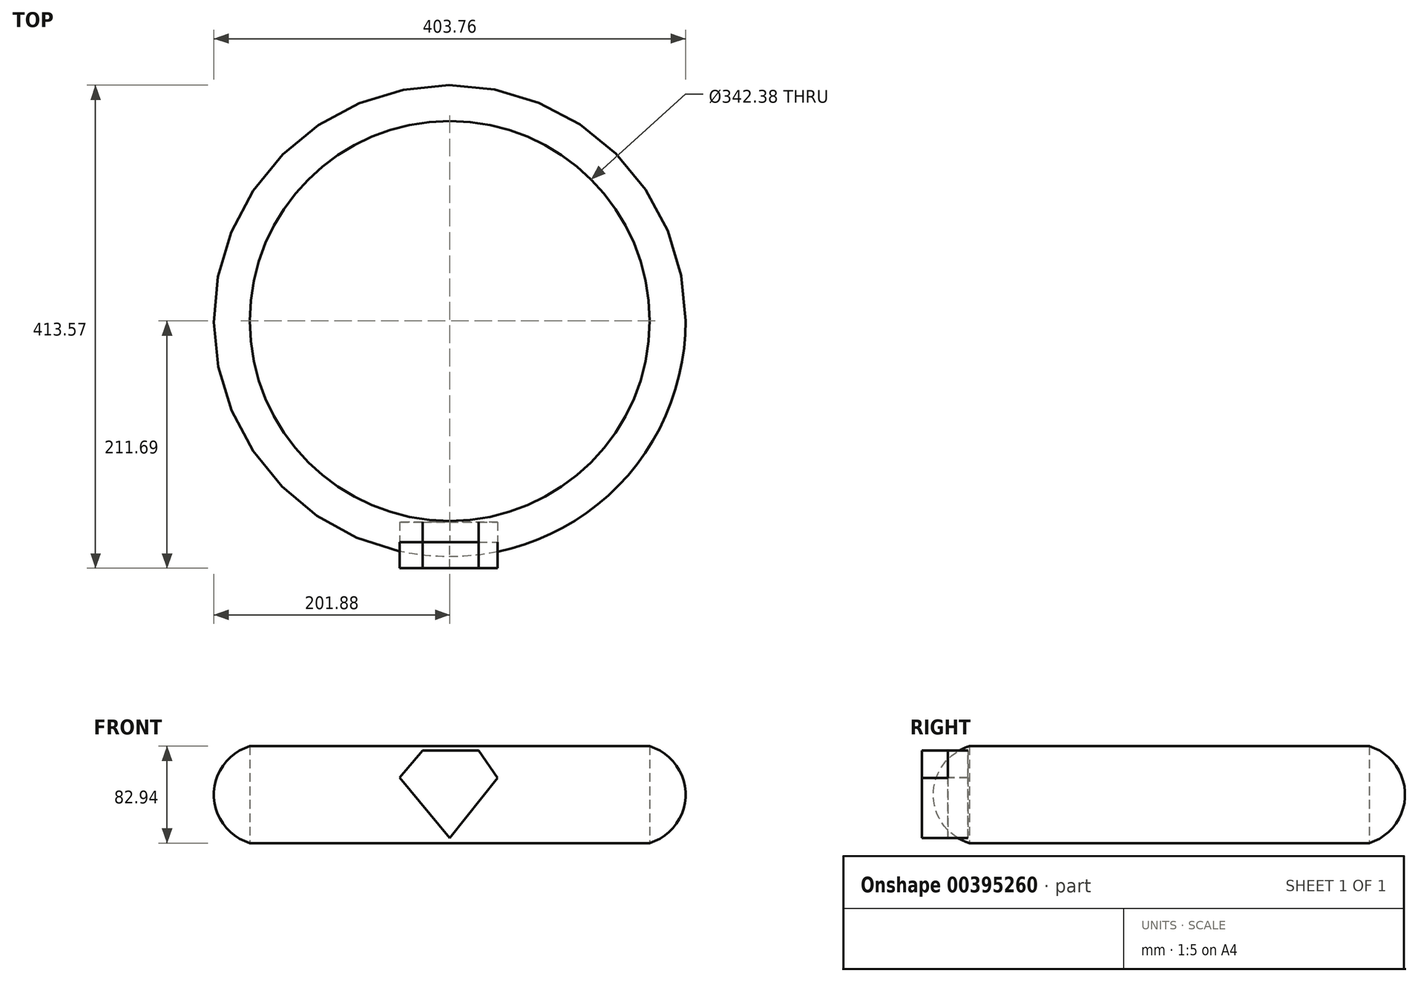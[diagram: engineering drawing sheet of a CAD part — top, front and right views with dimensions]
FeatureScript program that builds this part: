
annotation { "Feature Type Name" : "Feature", "Feature Type Description" : "" }
export const myFeature = defineFeature(function(context is Context, id is Id, definition is map)
    precondition{}
    {
        {
            var Q0;
            Q0=qCreatedBy(makeId("Top.planeOp"),FACE);
            var sketch = newSketch(context, id + "F0", { "sketchPlane" : qUnion([Q0])});
            skCircle(sketch, "E0", {"center": v(0, 0) * mm, "radius": 206.66 * mm});
            skSolve(sketch);
        }
        {
            var Q0;
            Q0=qCreatedBy(makeId("Right.planeOp"),FACE);
            var sketch = newSketch(context, id + "F1", { "sketchPlane" : qUnion([Q0])});
            skCircle(sketch, "E1", {"center": v(-158.53, 0) * mm, "radius": 43.36 * mm});
            skSolve(sketch);
        }
        {
            var Q0;
            Q0=makeQuery(id+"F1.imprint","IMPRINT",FACE,{"disambiguationData":[TD([[makeQuery(id+"F1.imprint","IMPRINT",EDGE,{"derivedFrom":sQuery(id+"F1.wireOp",EDGE,"E1")}),1.0]])]});
            var Q1;
            Q1=sQuery(id+"F0.wireOp",EDGE,"E0");
            sweep(context, id + "F2", {"profiles" : qUnion([Q0]), "path" : qUnion([Q1])});
        }
        {
            var Q0;
            Q0=qCreatedBy(makeId("Top.planeOp"),FACE);
            var sketch = newSketch(context, id + "F3", { "sketchPlane" : qUnion([Q0])});
            skCircle(sketch, "E2", {"center": v(0, 0) * mm, "radius": 171.19 * mm});
            skSolve(sketch);
        }
        {
            var Q0;
            Q0=qSketchRegion(id+"F3",true);
            extrude(context, id + "F4", {"entities" : qUnion([Q0]), "operationType" : NewBodyOperationType.REMOVE, "depth" : 439.93 * mm, "hasSecondDirection" : true, "secondDirectionOppositeDirection" : true, "secondDirectionDepth" : 259.08 * mm});
        }
        {
            var Q0;
            Q0=qCreatedBy(makeId("Top.planeOp"),FACE);
            var sketch = newSketch(context, id + "F5", { "sketchPlane" : qUnion([Q0])});
            skLineSegment(sketch, "E3", {"start": v(-284, -44.23) * mm, "end": v(-276.12, -35.04) * mm});
            skLineSegment(sketch, "E4", {"start": v(-276.12, -35.04) * mm, "end": v(-257.04, -35.04) * mm});
            skLineSegment(sketch, "E5", {"start": v(-257.04, -35.04) * mm, "end": v(-250.46, -44.36) * mm});
            skLineSegment(sketch, "E6", {"start": v(-250.46, -44.36) * mm, "end": v(-266.84, -65) * mm});
            skLineSegment(sketch, "E7", {"start": v(-266.84, -65) * mm, "end": v(-284, -44.23) * mm});
            skSolve(sketch);
        }
        {
            var Q0;
            Q0=qSketchRegion(id+"F5",true);
            extrude(context, id + "F6", {"entities" : qUnion([Q0]), "depth" : 8.9 * mm});
        }
        {
            var Q0;
            Q0=makeQuery(id+"F6.opExtrude","SWEPT_BODY",BODY,{"disambiguationData":[OSD([sQuery(id+"F5.wireOp",EDGE,"E3"),sQuery(id+"F5.wireOp",EDGE,"E4"),sQuery(id+"F5.wireOp",EDGE,"E5"),sQuery(id+"F5.wireOp",EDGE,"E6"),sQuery(id+"F5.wireOp",EDGE,"E7")])]});
            var Q1;
            Q1=makeQuery(id+"F6.opExtrude","CAP_EDGE",EDGE,{"disambiguationData":[OSD([sQuery(id+"F5.wireOp",EDGE,"E4")])],"isStart":false});
            transform(context, id + "F7", {"entities" : qUnion([Q0]), "transformType" : TransformType.ROTATION, "transformAxis" : qUnion([Q1]), "angle" : 90 * degree, "makeCopy" : false});
        }
        {
            var Q0;
            Q0=makeQuery(id+"F6.opExtrude","SWEPT_BODY",BODY,{"disambiguationData":[OSD([sQuery(id+"F5.wireOp",EDGE,"E3"),sQuery(id+"F5.wireOp",EDGE,"E4"),sQuery(id+"F5.wireOp",EDGE,"E5"),sQuery(id+"F5.wireOp",EDGE,"E6"),sQuery(id+"F5.wireOp",EDGE,"E7")])]});
            transform(context, id + "F8", {"entities" : qUnion([Q0]), "transformType" : TransformType.TRANSLATION_3D, "dx" : 273.3 * mm, "dy" : -174.5 * mm, "dz" : -10.67 * mm, "makeCopy" : false});
        }
        {
            var Q0;
            Q0=makeQuery(id+"F6.opExtrude","SWEPT_BODY",BODY,{"disambiguationData":[OSD([sQuery(id+"F5.wireOp",EDGE,"E3"),sQuery(id+"F5.wireOp",EDGE,"E4"),sQuery(id+"F5.wireOp",EDGE,"E5"),sQuery(id+"F5.wireOp",EDGE,"E6"),sQuery(id+"F5.wireOp",EDGE,"E7")])]});
            var Q1;
            Q1=qCreatedBy(makeId("Origin.pointOp"),VERTEX);
            transform(context, id + "F9", {"entities" : qUnion([Q0]), "transformType" : TransformType.SCALE_UNIFORMLY, "scale" : 2.5, "scalePoint" : qUnion([Q1]), "makeCopy" : false});
        }
        {
            var Q0;
            Q0=makeQuery(id+"F6.opExtrude","SWEPT_BODY",BODY,{"disambiguationData":[OSD([sQuery(id+"F5.wireOp",EDGE,"E3"),sQuery(id+"F5.wireOp",EDGE,"E4"),sQuery(id+"F5.wireOp",EDGE,"E5"),sQuery(id+"F5.wireOp",EDGE,"E6"),sQuery(id+"F5.wireOp",EDGE,"E7")])]});
            transform(context, id + "F10", {"entities" : qUnion([Q0]), "transformType" : TransformType.TRANSLATION_3D, "dx" : -16 * mm, "dy" : 312.17 * mm, "dz" : 42.16 * mm, "makeCopy" : false});
        }
        {
            var Q0;
            Q0=makeQuery(id+"F6.opExtrude","CAP_FACE",FACE,{"disambiguationData":[OSD([sQuery(id+"F5.wireOp",EDGE,"E3"),sQuery(id+"F5.wireOp",EDGE,"E4"),sQuery(id+"F5.wireOp",EDGE,"E5"),sQuery(id+"F5.wireOp",EDGE,"E6"),sQuery(id+"F5.wireOp",EDGE,"E7")])],"isStart":true});
            extrude(context, id + "F11", {"entities" : qUnion([Q0]), "depth" : 17.27 * mm});
        }
    });
